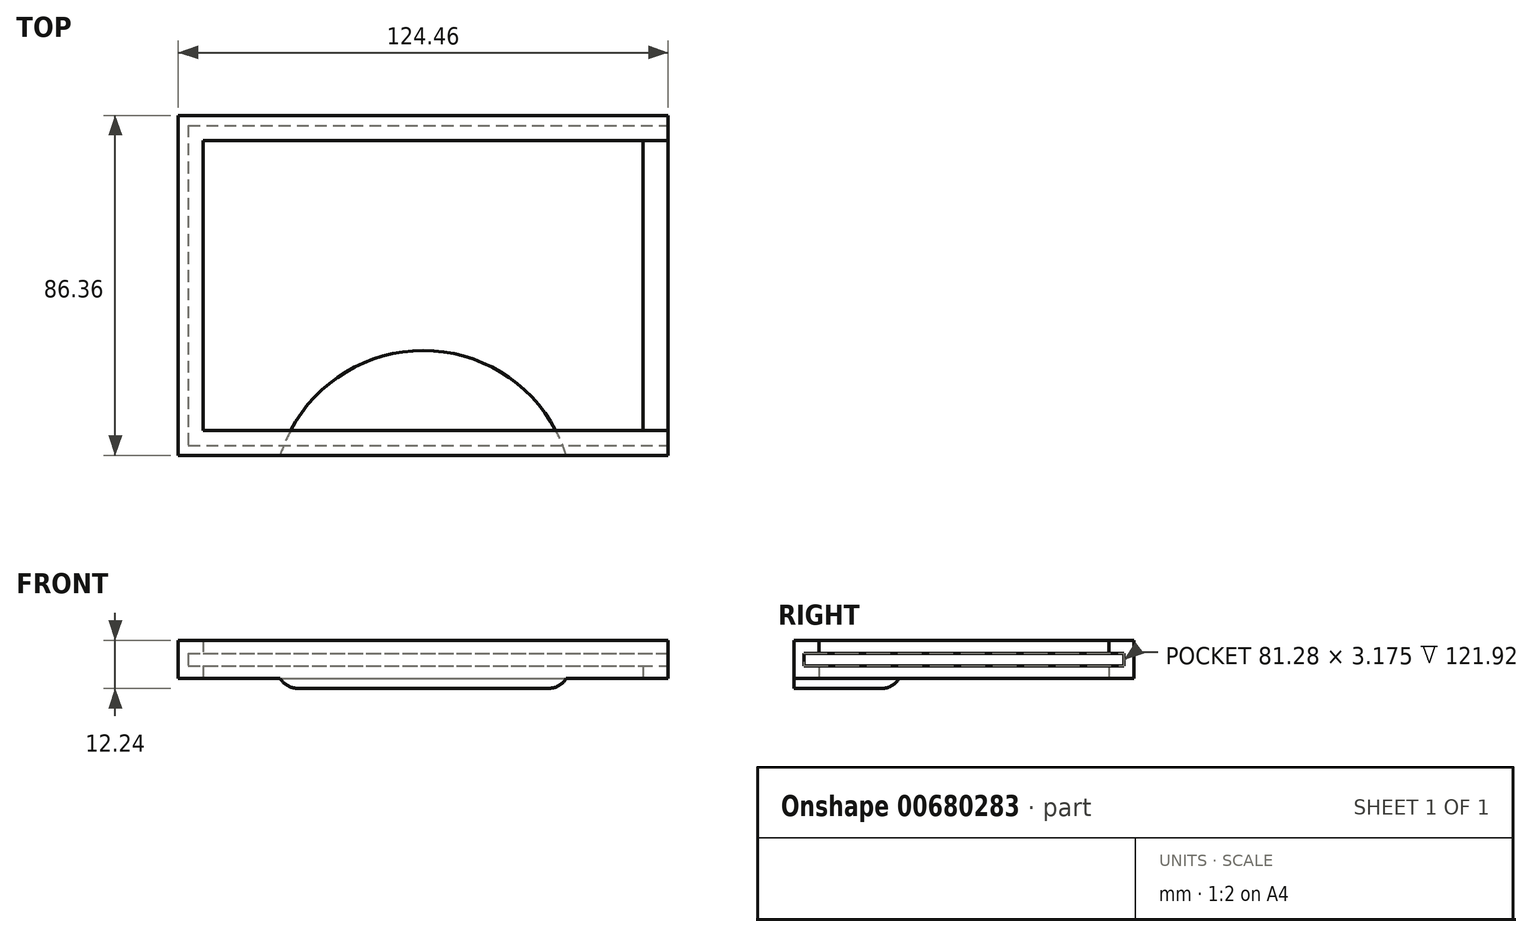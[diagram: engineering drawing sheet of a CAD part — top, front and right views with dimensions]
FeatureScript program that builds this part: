
annotation { "Feature Type Name" : "Feature", "Feature Type Description" : "" }
export const myFeature = defineFeature(function(context is Context, id is Id, definition is map)
    precondition{}
    {
        {
            var Q0;
            Q0=qCreatedBy(makeId("Top.planeOp"),FACE);
            var sketch = newSketch(context, id + "F0", { "sketchPlane" : qUnion([Q0])});
            skLineSegment(sketch, "E0.bottom", {"start": v(-55.88, 36.83) * mm, "end": v(55.88, 36.83) * mm});
            skLineSegment(sketch, "E0.top", {"start": v(-55.88, -36.83) * mm, "end": v(55.88, -36.83) * mm});
            skLineSegment(sketch, "E0.left", {"start": v(-55.88, 36.83) * mm, "end": v(-55.88, -36.83) * mm});
            skLineSegment(sketch, "E0.right", {"start": v(55.88, 36.83) * mm, "end": v(55.88, -36.83) * mm});
            skPoint(sketch, "E0.middle", {"position": v(0, 0) * mm});
            skLineSegment(sketch, "E1.bottom", {"start": v(-59.7, 40.64) * mm, "end": v(59.7, 40.64) * mm});
            skLineSegment(sketch, "E1.top", {"start": v(-59.7, -40.64) * mm, "end": v(59.7, -40.64) * mm});
            skLineSegment(sketch, "E1.left", {"start": v(-59.7, 40.64) * mm, "end": v(-59.7, -40.64) * mm});
            skLineSegment(sketch, "E1.right", {"start": v(59.7, 40.64) * mm, "end": v(59.7, -40.64) * mm});
            skLineSegment(sketch, "E2.bottom", {"start": v(-62.23, 43.18) * mm, "end": v(62.23, 43.18) * mm});
            skLineSegment(sketch, "E2.top", {"start": v(-62.23, -43.18) * mm, "end": v(62.23, -43.18) * mm});
            skLineSegment(sketch, "E2.left", {"start": v(-62.23, 43.18) * mm, "end": v(-62.23, -43.18) * mm});
            skLineSegment(sketch, "E2.right", {"start": v(62.23, 43.18) * mm, "end": v(62.23, -43.18) * mm});
            skLineSegment(sketch, "E3", {"start": v(59.7, 40.64) * mm, "end": v(62.23, 40.64) * mm});
            skLineSegment(sketch, "E4", {"start": v(55.88, 36.83) * mm, "end": v(62.23, 36.83) * mm});
            skLineSegment(sketch, "E5", {"start": v(55.88, -36.83) * mm, "end": v(62.23, -36.83) * mm});
            skLineSegment(sketch, "E6", {"start": v(59.7, -40.64) * mm, "end": v(62.23, -40.64) * mm});
            skSolve(sketch);
        }
        {
            var Q0;
            Q0=makeQuery(id+"F0.imprint","IMPRINT",FACE,{"disambiguationData":[TD([[makeQuery(id+"F0.imprint","IMPRINT",EDGE,{"derivedFrom":sQuery(id+"F0.wireOp",EDGE,"E0.bottom")}),1.0]])]});
            var Q1;
            {var subQ0=sQuery(id+"F0.wireOp",EDGE,"E3");Q1=makeQuery(id+"F0.imprint","IMPRINT",FACE,{"disambiguationData":[TD([[makeQuery(id+"F0.imprint","IMPRINT",EDGE,{"derivedFrom":subQ0}),-1.0]])]});}
            var Q2;
            {var subQ0=sQuery(id+"F0.wireOp",EDGE,"E6");Q2=makeQuery(id+"F0.imprint","IMPRINT",FACE,{"disambiguationData":[TD([[makeQuery(id+"F0.imprint","IMPRINT",EDGE,{"derivedFrom":subQ0}),1.0]])]});}
            var Q3;
            {var subQ0=sQuery(id+"F0.wireOp",EDGE,"E0.right");Q3=makeQuery(id+"F0.imprint","IMPRINT",FACE,{"disambiguationData":[TD([[makeQuery(id+"F0.imprint","IMPRINT",EDGE,{"derivedFrom":subQ0}),1.0]])]});}
            var Q4;
            {var subQ0=sQuery(id+"F0.wireOp",EDGE,"E4");var subQ1=sQuery(id+"F0.wireOp",EDGE,"E1.right");var subQ2=makeQuery(id+"F0.imprint","INTERSECT",VERTEX,{"derivedFrom":[subQ1,subQ0]});Q4=makeQuery(id+"F0.imprint","IMPRINT",FACE,{"disambiguationData":[TD([[makeQuery(id+"F0.imprint","IMPRINT",EDGE,{"disambiguationData":[TD([[subQ2,-1.0]])],"derivedFrom":subQ1}),1.0]])]});}
            extrude(context, id + "F1", {"entities" : qUnion([Q0, Q1, Q2, Q3, Q4]), "depth" : 3.17 * mm});
        }
        {
            var Q0;
            Q0=makeQuery(id+"F0.imprint","IMPRINT",FACE,{"disambiguationData":[TD([[makeQuery(id+"F0.imprint","IMPRINT",EDGE,{"derivedFrom":sQuery(id+"F0.wireOp",EDGE,"E1.bottom")}),1.0]])]});
            extrude(context, id + "F2", {"entities" : qUnion([Q0]), "operationType" : NewBodyOperationType.ADD, "depth" : 9.7 * mm});
        }
        {
            var Q0;
            {var subQ2=sQuery(id+"F0.wireOp",EDGE,"E0.bottom");Q0=makeQuery(id+"F0.imprint","IMPRINT",FACE,{"disambiguationData":[TD([[makeQuery(id+"F0.imprint","IMPRINT",EDGE,{"derivedFrom":subQ2}),1.0]])]});}
            var Q1;
            {var subQ0=sQuery(id+"F0.wireOp",EDGE,"E6");Q1=makeQuery(id+"F0.imprint","IMPRINT",FACE,{"disambiguationData":[TD([[makeQuery(id+"F0.imprint","IMPRINT",EDGE,{"derivedFrom":subQ0}),1.0]])]});}
            var Q2;
            {var subQ0=sQuery(id+"F0.wireOp",EDGE,"E3");Q2=makeQuery(id+"F0.imprint","IMPRINT",FACE,{"disambiguationData":[TD([[makeQuery(id+"F0.imprint","IMPRINT",EDGE,{"derivedFrom":subQ0}),-1.0]])]});}
            extrude(context, id + "F3", {"entities" : qUnion([Q0, Q1, Q2]), "operationType" : NewBodyOperationType.ADD, "depth" : 9.7 * mm, "hasSecondDirection" : true, "secondDirectionOppositeDirection" : true, "secondDirectionDepth" : -6.35 * mm});
        }
        {
            var Q0;
            {var subQ0=sQuery(id+"F0.wireOp",EDGE,"E6");var subQ1=sQuery(id+"F0.wireOp",EDGE,"E3");var subQ2=sQuery(id+"F0.wireOp",EDGE,"E2.right");var subQ3=sQuery(id+"F0.wireOp",EDGE,"E1.left");var subQ4=sQuery(id+"F0.wireOp",EDGE,"E1.top");var subQ5=sQuery(id+"F0.wireOp",EDGE,"E1.bottom");Q0=makeQuery(id+"F2.boolean.opBoolean","MERGE",FACE,{"derivedFrom":[makeQuery(id+"F1.opExtrude","CAP_FACE",FACE,{"disambiguationData":[OSD([sQuery(id+"F0.wireOp",EDGE,"E0.bottom"),sQuery(id+"F0.wireOp",EDGE,"E0.top"),sQuery(id+"F0.wireOp",EDGE,"E0.left"),sQuery(id+"F0.wireOp",EDGE,"E0.right"),subQ5,subQ4,subQ3,subQ2,subQ1,subQ0])],"isStart":true}),makeQuery(id+"F2.opExtrude","CAP_FACE",FACE,{"disambiguationData":[OSD([subQ5,subQ4,subQ3,sQuery(id+"F0.wireOp",EDGE,"E2.bottom"),sQuery(id+"F0.wireOp",EDGE,"E2.top"),sQuery(id+"F0.wireOp",EDGE,"E2.left"),subQ2,subQ1,subQ0])],"isStart":true})]});}
            var sketch = newSketch(context, id + "F4", { "sketchPlane" : qUnion([Q0])});
            skArc(sketch, "E7", {"start": v(-36.33, 43.18) * mm, "mid": v(0, 16.55) * mm, "end": v(36.33, 43.18) * mm});
            skSolve(sketch);
        }
        {
            var Q0;
            {var subQ0=sQuery(id+"F4.wireOp",EDGE,"E7");var subQ1=makeQuery(id+"F1.opExtrude","CAP_EDGE",EDGE,{"disambiguationData":[OSD([sQuery(id+"F0.wireOp",EDGE,"E0.top")])],"isStart":true});var subQ2=makeQuery(id+"F4.imprint","INTERSECT",VERTEX,{"disambiguationData":[OD(0.0)],"derivedFrom":[subQ1,subQ0]});Q0=makeQuery(id+"F4.imprint","IMPRINT",FACE,{"disambiguationData":[TD([[makeQuery(id+"F4.imprint","IMPRINT",EDGE,{"disambiguationData":[TD([[subQ2,-1.0]])],"derivedFrom":subQ0}),1.0]])]});}
            var Q1;
            {var subQ0=sQuery(id+"F4.wireOp",EDGE,"E7");var subQ1=makeQuery(id+"F2.opExtrude","CAP_EDGE",EDGE,{"disambiguationData":[OSD([sQuery(id+"F0.wireOp",EDGE,"E2.top")])],"isStart":true});var subQ2=makeQuery(id+"F4.imprint","INTERSECT",VERTEX,{"disambiguationData":[OD(0.0)],"derivedFrom":[subQ1,subQ0]});Q1=makeQuery(id+"F4.imprint","IMPRINT",FACE,{"disambiguationData":[TD([[makeQuery(id+"F4.imprint","IMPRINT",EDGE,{"disambiguationData":[TD([[subQ2,-1.0]])],"derivedFrom":subQ0}),1.0]])]});}
            extrude(context, id + "F5", {"entities" : qUnion([Q0, Q1]), "operationType" : NewBodyOperationType.ADD, "depth" : 2.54 * mm, "offsetDistance" : 25.4 * mm});
        }
        {
            var Q0;
            Q0=makeQuery(id+"F5.opExtrude","CAP_EDGE",EDGE,{"disambiguationData":[OSD([sQuery(id+"F4.wireOp",EDGE,"E7")])],"isStart":false});
            fillet(context, id + "F6", {"entities" : qUnion([Q0]), "radius" : 5.08 * mm, "tangentPropagation" : true, "allowEdgeOverflow" : false});
        }
    });
